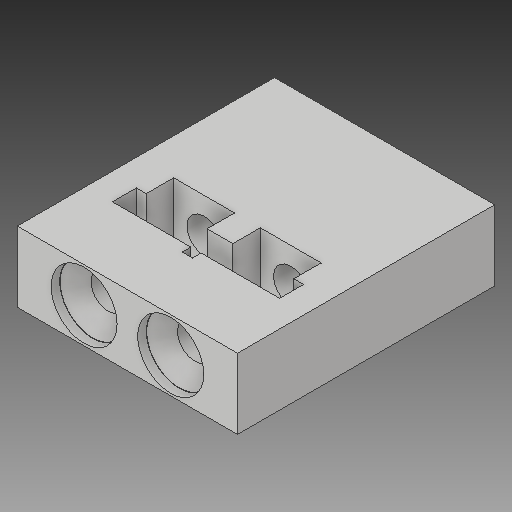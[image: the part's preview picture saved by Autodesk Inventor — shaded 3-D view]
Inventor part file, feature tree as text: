
AUTODESK INVENTOR PART (.ipt)
format: ipt  version: 2020 (Build 240168000, 168)  size: 174,592 bytes
history: native  units: mm
features: extrude x4, sketch x4, other x2, chamfer x1
ambient origin geometry x8: Origin, YZ Plane, XZ Plane, XY Plane, X Axis, Y Axis, Z Axis, Center Point
bodies: Solide1 (feature_tree)
feature tree (11):
  extrude  "Extrusion1"  Depth=75.0mm
  extrude  "Extrusion2"  Depth=19.5mm
  extrude  "Extrusion3"  Depth=2.8mm
  chamfer  "Chanfrein1"  Distance=8.0mm
  other  "Axe de construction1"
  other  "Axe de construction2"
  extrude  "Extrusion4"  Depth=8.2mm TaperAngle=0.0deg
  sketch  "Esquisse1"
  sketch  "Esquisse2"
  sketch  "Esquisse3"
  sketch  "Esquisse5"
